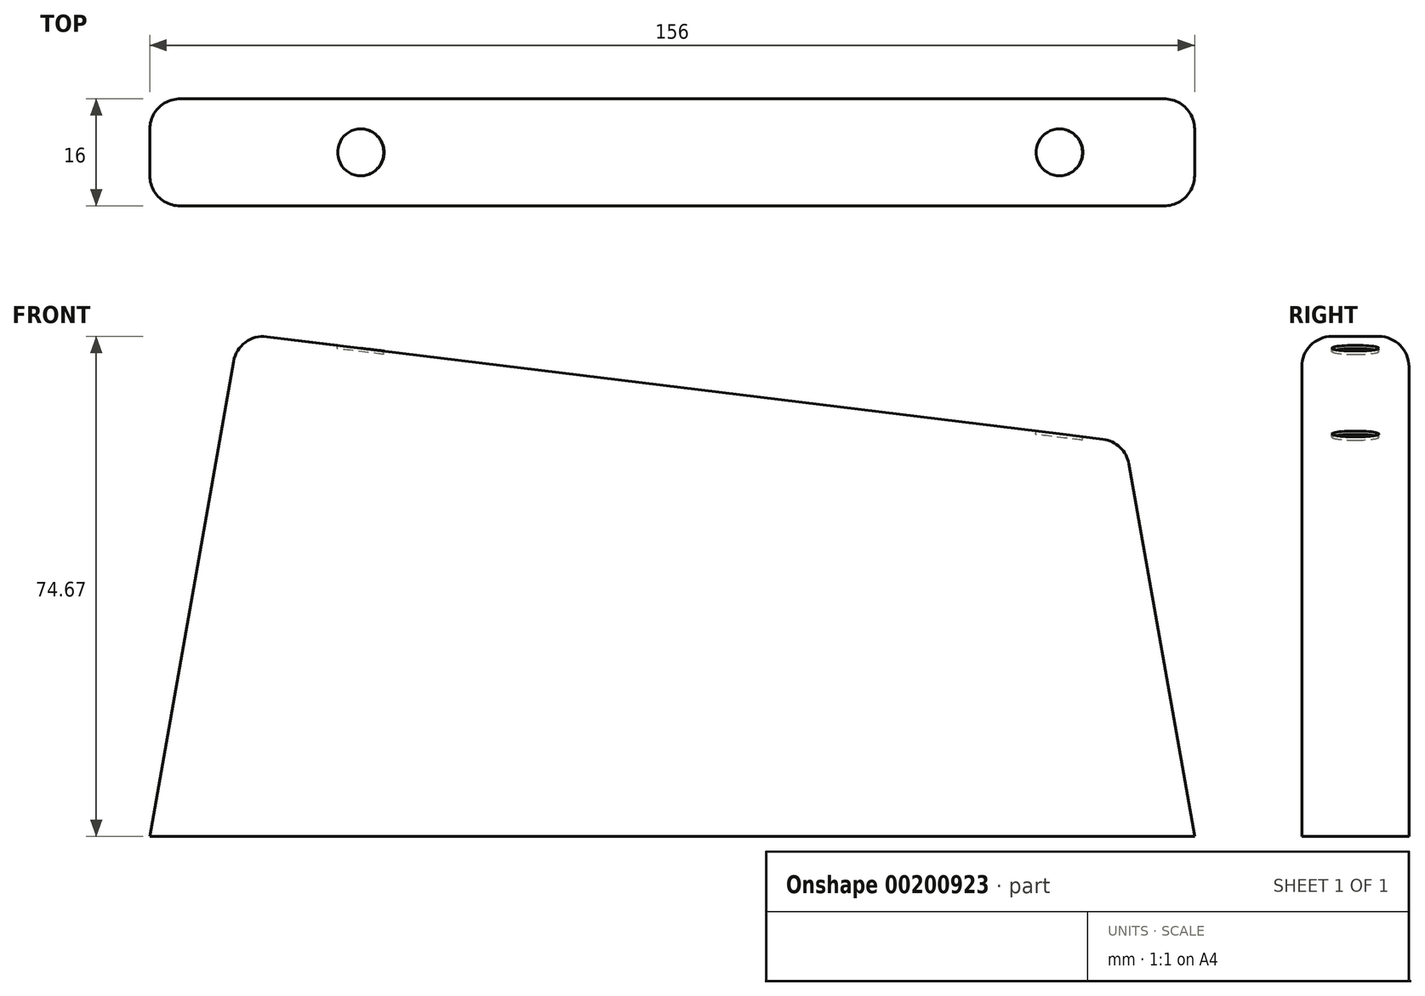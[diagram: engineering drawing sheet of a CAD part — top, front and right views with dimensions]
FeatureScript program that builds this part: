
annotation { "Feature Type Name" : "Feature", "Feature Type Description" : "" }
export const myFeature = defineFeature(function(context is Context, id is Id, definition is map)
    precondition{}
    {
        {
            var Q0;
            Q0=qCreatedBy(makeId("Front.planeOp"),FACE);
            var sketch = newSketch(context, id + "F0", { "sketchPlane" : qUnion([Q0])});
            skLineSegment(sketch, "E0", {"start": v(-69.5, 0) * mm, "end": v(86.5, 0) * mm});
            skLineSegment(sketch, "E1", {"start": v(86.5, 0) * mm, "end": v(76.1, 58.9) * mm});
            skLineSegment(sketch, "E2", {"start": v(76.1, 58.9) * mm, "end": v(-56.25, 75.16) * mm});
            skLineSegment(sketch, "E3", {"start": v(-56.25, 75.16) * mm, "end": v(-69.5, 0) * mm});
            skSolve(sketch);
        }
        {
            var Q0;
            Q0=makeQuery(id+"F0.imprint","IMPRINT",FACE,{"disambiguationData":[TD([[makeQuery(id+"F0.imprint","IMPRINT",EDGE,{"derivedFrom":sQuery(id+"F0.wireOp",EDGE,"E0")}),1.0]])]});
            extrude(context, id + "F1", {"entities" : qUnion([Q0]), "depth" : 16 * mm, "offsetDistance" : 25 * mm});
        }
        {
            var Q0;
            Q0=makeQuery(id+"F1.opExtrude","SWEPT_FACE",FACE,{"disambiguationData":[OSD([sQuery(id+"F0.wireOp",EDGE,"E2")])]});
            var sketch = newSketch(context, id + "F2", { "sketchPlane" : qUnion([Q0])});
            skCircle(sketch, "E4", {"center": v(-46.6, -8) * mm, "radius": 3.5 * mm});
            skPoint(sketch, "E4.centerSnap0", {"position": v(-65, -8) * mm});
            skCircle(sketch, "E5", {"center": v(58.5, -8) * mm, "radius": 3.5 * mm});
            skPoint(sketch, "E5.centerSnap0", {"position": v(68.36, -8) * mm});
            skSolve(sketch);
        }
        {
            var Q0;
            Q0=makeQuery(id+"F2.imprint","IMPRINT",FACE,{"disambiguationData":[TD([[makeQuery(id+"F2.imprint","IMPRINT",EDGE,{"derivedFrom":sQuery(id+"F2.wireOp",EDGE,"E4")}),1.0]])]});
            var Q1;
            Q1=makeQuery(id+"F2.imprint","IMPRINT",FACE,{"disambiguationData":[TD([[makeQuery(id+"F2.imprint","IMPRINT",EDGE,{"derivedFrom":sQuery(id+"F2.wireOp",EDGE,"E5")}),1.0]])]});
            extrude(context, id + "F3", {"entities" : qUnion([Q0, Q1]), "operationType" : NewBodyOperationType.REMOVE, "oppositeDirection" : true, "depth" : 0.5 * mm, "offsetDistance" : 25 * mm});
        }
        {
            var Q0;
            Q0=makeQuery(id+"F1.opExtrude","CAP_EDGE",EDGE,{"disambiguationData":[OSD([sQuery(id+"F0.wireOp",EDGE,"E2")])],"isStart":false});
            var Q1;
            Q1=makeQuery(id+"F1.opExtrude","CAP_EDGE",EDGE,{"disambiguationData":[OSD([sQuery(id+"F0.wireOp",EDGE,"E2")])],"isStart":true});
            var Q2;
            Q2=makeQuery(id+"F1.opExtrude","CAP_EDGE",EDGE,{"disambiguationData":[OSD([sQuery(id+"F0.wireOp",EDGE,"E1")])],"isStart":true});
            var Q3;
            Q3=makeQuery(id+"F1.opExtrude","CAP_EDGE",EDGE,{"disambiguationData":[OSD([sQuery(id+"F0.wireOp",EDGE,"E1")])],"isStart":false});
            var Q4;
            Q4=makeQuery(id+"F1.opExtrude","CAP_EDGE",EDGE,{"disambiguationData":[OSD([sQuery(id+"F0.wireOp",EDGE,"E3")])],"isStart":false});
            var Q5;
            Q5=makeQuery(id+"F1.opExtrude","CAP_EDGE",EDGE,{"disambiguationData":[OSD([sQuery(id+"F0.wireOp",EDGE,"E3")])],"isStart":true});
            var Q6;
            Q6=makeQuery(id+"F1.opExtrude","SWEPT_EDGE",EDGE,{"disambiguationData":[OSD([sQuery(id+"F0.wireOp",EDGE,"E2"),sQuery(id+"F0.wireOp",EDGE,"E3")])]});
            var Q7;
            Q7=makeQuery(id+"F1.opExtrude","SWEPT_EDGE",EDGE,{"disambiguationData":[OSD([sQuery(id+"F0.wireOp",EDGE,"E1"),sQuery(id+"F0.wireOp",EDGE,"E2")])]});
            fillet(context, id + "F4", {"entities" : qUnion([Q0, Q1, Q2, Q3, Q4, Q5, Q6, Q7]), "radius" : 4.5 * mm, "tangentPropagation" : true, "allowEdgeOverflow" : false});
        }
    });
